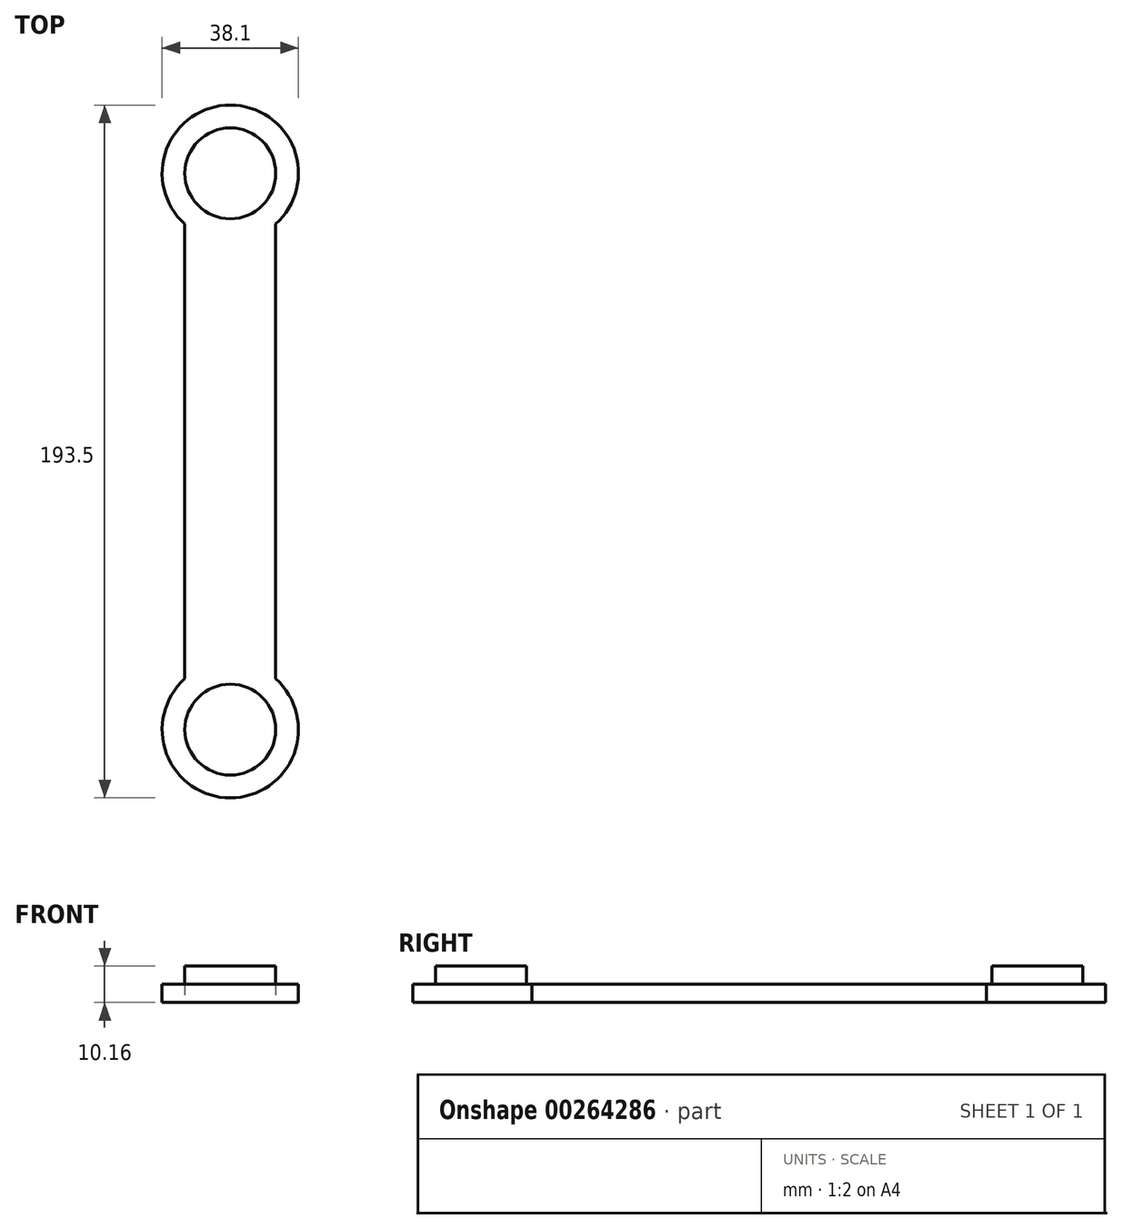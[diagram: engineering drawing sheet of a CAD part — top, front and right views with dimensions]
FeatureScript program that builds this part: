
annotation { "Feature Type Name" : "Feature", "Feature Type Description" : "" }
export const myFeature = defineFeature(function(context is Context, id is Id, definition is map)
    precondition{}
    {
        {
            var Q0;
            Q0=qCreatedBy(makeId("Top.planeOp"),FACE);
            var sketch = newSketch(context, id + "F0", { "sketchPlane" : qUnion([Q0])});
            skLineSegment(sketch, "E0.bottom", {"start": v(0, 0) * mm, "end": v(25.4, 0) * mm});
            skLineSegment(sketch, "E0.top", {"start": v(0, 127) * mm, "end": v(25.4, 127) * mm});
            skLineSegment(sketch, "E0.left", {"start": v(0, 0) * mm, "end": v(0, 127) * mm});
            skLineSegment(sketch, "E0.right", {"start": v(25.4, 0) * mm, "end": v(25.4, 127) * mm});
            skCircle(sketch, "E1", {"center": v(12.7, 141.2) * mm, "radius": 19.05 * mm});
            skPoint(sketch, "E1.third.point", {"position": v(12.7, 160.25) * mm});
            skPoint(sketch, "E1.third.point.positionSnap0", {"position": v(12.7, 127) * mm});
            skCircle(sketch, "E2", {"center": v(12.7, -14.2) * mm, "radius": 19.05 * mm});
            skPoint(sketch, "E2.third.point", {"position": v(12.7, -33.25) * mm});
            skPoint(sketch, "E2.third.point.positionSnap0", {"position": v(12.7, 0) * mm});
            skSolve(sketch);
        }
        {
            var Q0;
            Q0 = qSketchRegion(id + "F0", true);
            extrude(context, id + "F1", {"entities" : qUnion([Q0]), "depth" : 5.08 * mm});
        }
        {
            var Q0;
            Q0=makeQuery(id+"F1.opExtrude","CAP_FACE",FACE,{"disambiguationData":[OSD([sQuery(id+"F0.wireOp",EDGE,"E0.left"),sQuery(id+"F0.wireOp",EDGE,"E0.right"),sQuery(id+"F0.wireOp",EDGE,"E1"),sQuery(id+"F0.wireOp",EDGE,"E2")])],"isStart":false});
            var sketch = newSketch(context, id + "F2", { "sketchPlane" : qUnion([Q0])});
            skCircle(sketch, "E3", {"center": v(12.7, -14.2) * mm, "radius": 12.7 * mm});
            skCircle(sketch, "E4", {"center": v(12.7, 141.2) * mm, "radius": 12.7 * mm});
            skSolve(sketch);
        }
        {
            var Q0;
            Q0=makeQuery(id+"F2.imprint","IMPRINT",FACE,{"disambiguationData":[TD([[makeQuery(id+"F2.imprint","IMPRINT",EDGE,{"derivedFrom":sQuery(id+"F2.wireOp",EDGE,"E3")}),1.0]])]});
            var Q1;
            Q1=makeQuery(id+"F2.imprint","IMPRINT",FACE,{"disambiguationData":[TD([[makeQuery(id+"F2.imprint","IMPRINT",EDGE,{"derivedFrom":sQuery(id+"F2.wireOp",EDGE,"E4")}),1.0]])]});
            extrude(context, id + "F3", {"entities" : qUnion([Q0, Q1]), "operationType" : NewBodyOperationType.ADD, "depth" : 5.08 * mm});
        }
    });
